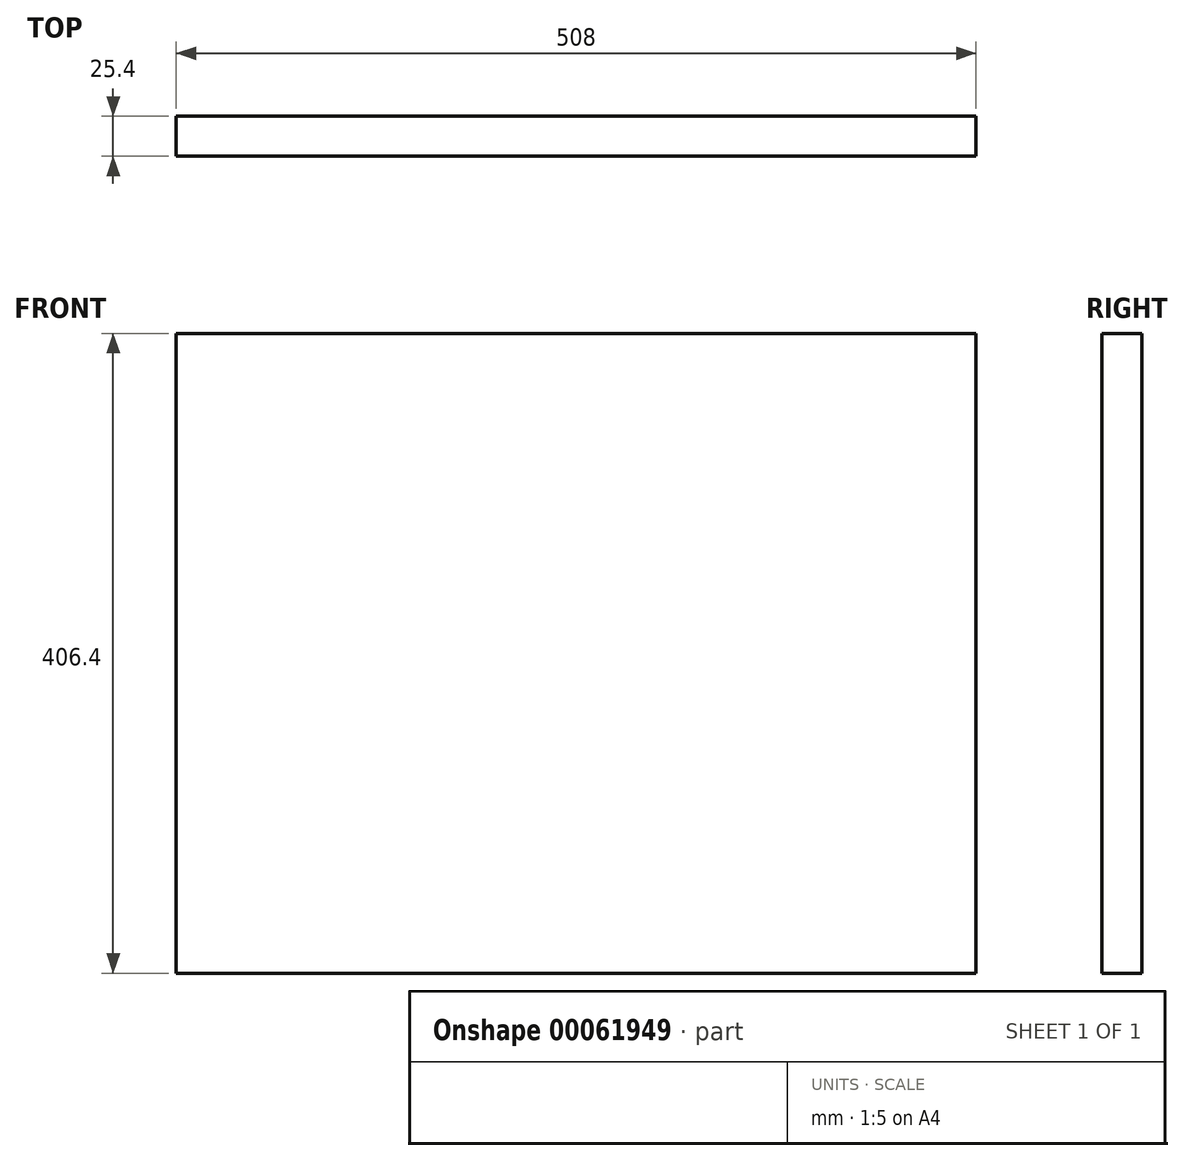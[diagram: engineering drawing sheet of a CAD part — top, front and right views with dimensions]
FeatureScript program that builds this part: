
annotation { "Feature Type Name" : "Feature", "Feature Type Description" : "" }
export const myFeature = defineFeature(function(context is Context, id is Id, definition is map)
    precondition{}
    {
        {
            var Q0;
            Q0=qCreatedBy(makeId("Front.planeOp"),FACE);
            var sketch = newSketch(context, id + "F0", { "sketchPlane" : qUnion([Q0])});
            skLineSegment(sketch, "E0.rect.bottom", {"start": v(254, -203.2) * mm, "end": v(-254, -203.2) * mm});
            skLineSegment(sketch, "E0.rect.top", {"start": v(254, 203.2) * mm, "end": v(-254, 203.2) * mm});
            skLineSegment(sketch, "E0.rect.left", {"start": v(254, -203.2) * mm, "end": v(254, 203.2) * mm});
            skLineSegment(sketch, "E0.rect.right", {"start": v(-254, -203.2) * mm, "end": v(-254, 203.2) * mm});
            skPoint(sketch, "E0.rect.middle", {"position": v(0, 0) * mm});
            skSolve(sketch);
        }
        {
            var Q0;
            Q0=makeQuery(id+"F0.imprint","IMPRINT",FACE,{"disambiguationData":[TD([[makeQuery(id+"F0.imprint","IMPRINT",EDGE,{"derivedFrom":sQuery(id+"F0.wireOp",EDGE,"E0.rect.bottom")}),-1.0]])]});
            extrude(context, id + "F1", {"entities" : qUnion([Q0]), "depth" : 25.4 * mm});
        }
    });
